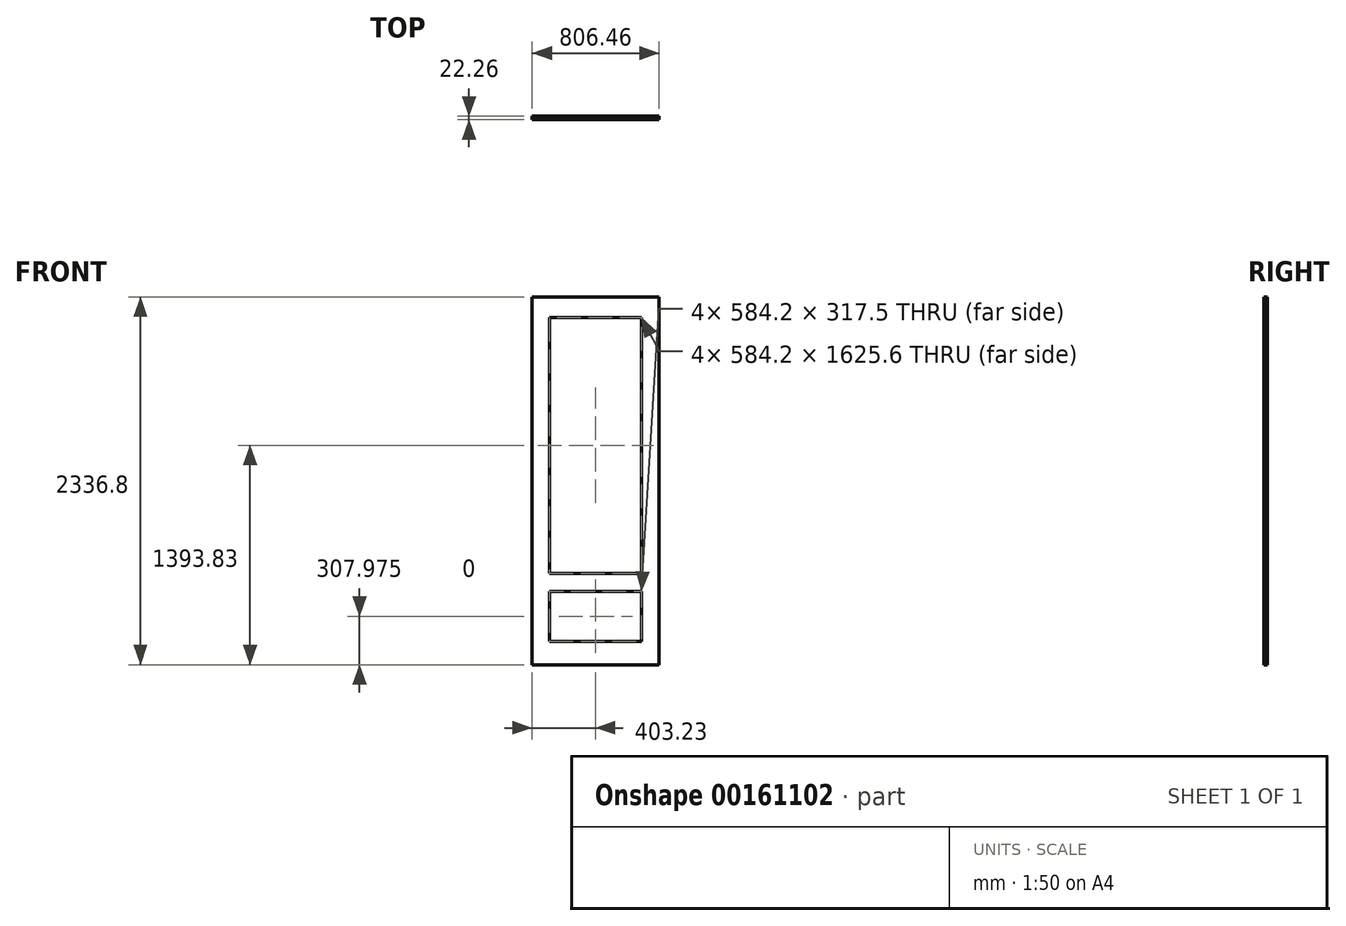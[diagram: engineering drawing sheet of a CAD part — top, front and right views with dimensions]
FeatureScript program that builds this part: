
annotation { "Feature Type Name" : "Feature", "Feature Type Description" : "" }
export const myFeature = defineFeature(function(context is Context, id is Id, definition is map)
    precondition{}
    {
        {
            var Q0;
            Q0=qCreatedBy(makeId("Front.planeOp"),FACE);
            var sketch = newSketch(context, id + "F0", { "sketchPlane" : qUnion([Q0])});
            skLineSegment(sketch, "E0.bottom", {"start": v(403.23, 1206.5) * mm, "end": v(-403.23, 1206.5) * mm});
            skLineSegment(sketch, "E0.top", {"start": v(403.23, -1206.5) * mm, "end": v(-403.23, -1206.5) * mm});
            skLineSegment(sketch, "E0.left", {"start": v(403.23, 1206.5) * mm, "end": v(403.23, -1206.5) * mm});
            skLineSegment(sketch, "E0.right", {"start": v(-403.23, 1206.5) * mm, "end": v(-403.23, -1206.5) * mm});
            skPoint(sketch, "E0.middle", {"position": v(0, 0) * mm});
            skLineSegment(sketch, "E1.bottom", {"start": v(-292.1, -663.58) * mm, "end": v(292.1, -663.58) * mm});
            skLineSegment(sketch, "E1.top", {"start": v(-292.1, -981.08) * mm, "end": v(292.1, -981.08) * mm});
            skLineSegment(sketch, "E1.left", {"start": v(-292.1, -663.58) * mm, "end": v(-292.1, -981.08) * mm});
            skLineSegment(sketch, "E1.right", {"start": v(292.1, -663.58) * mm, "end": v(292.1, -981.08) * mm});
            skLineSegment(sketch, "E2.bottom", {"start": v(-292.1, 1076.33) * mm, "end": v(292.1, 1076.33) * mm});
            skLineSegment(sketch, "E2.top", {"start": v(-292.1, -549.27) * mm, "end": v(292.1, -549.27) * mm});
            skLineSegment(sketch, "E2.left", {"start": v(-292.1, 1076.33) * mm, "end": v(-292.1, -549.27) * mm});
            skLineSegment(sketch, "E2.right", {"start": v(292.1, 1076.33) * mm, "end": v(292.1, -549.27) * mm});
            skSolve(sketch);
        }
        {
            var Q0;
            Q0=qSketchRegion(id+"F0",true);
            extrude(context, id + "F1", {"entities" : qUnion([Q0]), "depth" : 22.22 * mm, "hasSecondDirection" : true, "secondDirectionOppositeDirection" : true, "secondDirectionDepth" : 1.75 / 50.8 * mm});
        }
        {
            var Q0;
            Q0=qCreatedBy(makeId("Front.planeOp"),FACE);
            var sketch = newSketch(context, id + "F2", { "sketchPlane" : qUnion([Q0])});
            skLineSegment(sketch, "E3.bottom", {"start": v(-561.43, 1477.6) * mm, "end": v(687.16, 1477.6) * mm});
            skLineSegment(sketch, "E3.top", {"start": v(-561.43, 1206.5) * mm, "end": v(687.16, 1206.5) * mm});
            skLineSegment(sketch, "E3.left", {"start": v(-561.43, 1477.6) * mm, "end": v(-561.43, 1206.5) * mm});
            skLineSegment(sketch, "E3.right", {"start": v(687.16, 1477.6) * mm, "end": v(687.16, 1206.5) * mm});
            skLineSegment(sketch, "E4.bottom", {"start": v(687.16, -1130.3) * mm, "end": v(-561.43, -1130.3) * mm});
            skLineSegment(sketch, "E4.top", {"start": v(687.16, -1634.32) * mm, "end": v(-561.43, -1634.32) * mm});
            skLineSegment(sketch, "E4.left", {"start": v(687.16, -1130.3) * mm, "end": v(687.16, -1634.32) * mm});
            skLineSegment(sketch, "E4.right", {"start": v(-561.43, -1130.3) * mm, "end": v(-561.43, -1634.32) * mm});
            skSolve(sketch);
        }
        {
            var Q0;
            Q0=qSketchRegion(id+"F2",true);
            extrude(context, id + "F3", {"entities" : qUnion([Q0]), "operationType" : NewBodyOperationType.REMOVE, "endBound" : BoundingType.THROUGH_ALL, "oppositeDirection" : true, "depth" : 25.4 * mm, "hasSecondDirection" : true, "secondDirectionBound" : SecondDirectionBoundingType.THROUGH_ALL, "secondDirectionOppositeDirection" : false, "secondDirectionDepth" : 25.4 * mm});
        }
    });
